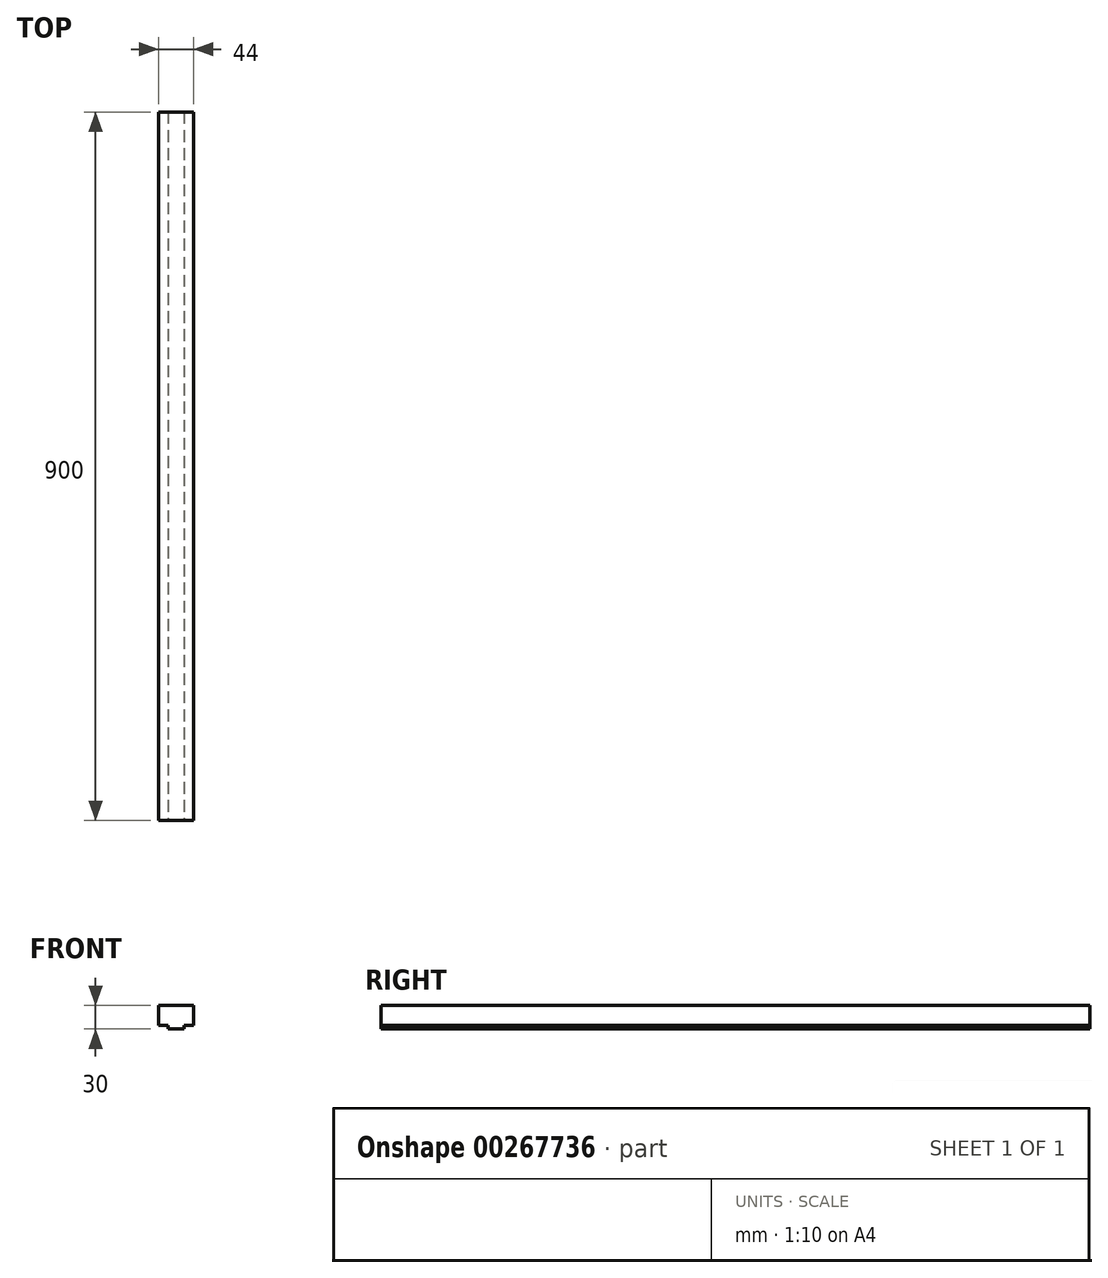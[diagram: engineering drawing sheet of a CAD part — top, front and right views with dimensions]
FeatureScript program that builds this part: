
annotation { "Feature Type Name" : "Feature", "Feature Type Description" : "" }
export const myFeature = defineFeature(function(context is Context, id is Id, definition is map)
    precondition{}
    {
        {
            var Q0;
            Q0=qCreatedBy(makeId("Front.planeOp"),FACE);
            var sketch = newSketch(context, id + "F0", { "sketchPlane" : qUnion([Q0])});
            skLineSegment(sketch, "E0.bottom", {"start": v(10, -15) * mm, "end": v(-10, -15) * mm});
            skLineSegment(sketch, "E0.top", {"start": v(22, 15) * mm, "end": v(-22, 15) * mm});
            skLineSegment(sketch, "E0.left", {"start": v(22, -10.4) * mm, "end": v(22, 15) * mm});
            skLineSegment(sketch, "E0.right", {"start": v(-22, -10.4) * mm, "end": v(-22, 15) * mm});
            skPoint(sketch, "E0.middle", {"position": v(0, 0) * mm});
            skLineSegment(sketch, "E1", {"start": v(0, -23.3) * mm, "end": v(-10, -23.3) * mm, "construction": true});
            skLineSegment(sketch, "E2", {"start": v(-10, -23.3) * mm, "end": v(-10, 2.5) * mm, "construction": true});
            skLineSegment(sketch, "E3", {"start": v(-10, 2.5) * mm, "end": v(10, 2.5) * mm, "construction": true});
            skLineSegment(sketch, "E4", {"start": v(10, 2.5) * mm, "end": v(10, -15) * mm, "construction": true});
            skLineSegment(sketch, "E5", {"start": v(-10, -15) * mm, "end": v(-10, -10.4) * mm});
            skLineSegment(sketch, "E6", {"start": v(-10, -10.4) * mm, "end": v(-22, -10.4) * mm});
            skLineSegment(sketch, "E7", {"start": v(10, -10.4) * mm, "end": v(22, -10.4) * mm});
            skLineSegment(sketch, "E8", {"start": v(10, -10.4) * mm, "end": v(10, -15) * mm});
            skPoint(sketch, "E9", {"position": v(0, 15) * mm});
            skSolve(sketch);
        }
        {
            var Q0;
            Q0=qSketchRegion(id+"F0",true);
            extrude(context, id + "F1", {"entities" : qUnion([Q0]), "oppositeDirection" : true, "depth" : 900 * mm});
        }
    });
